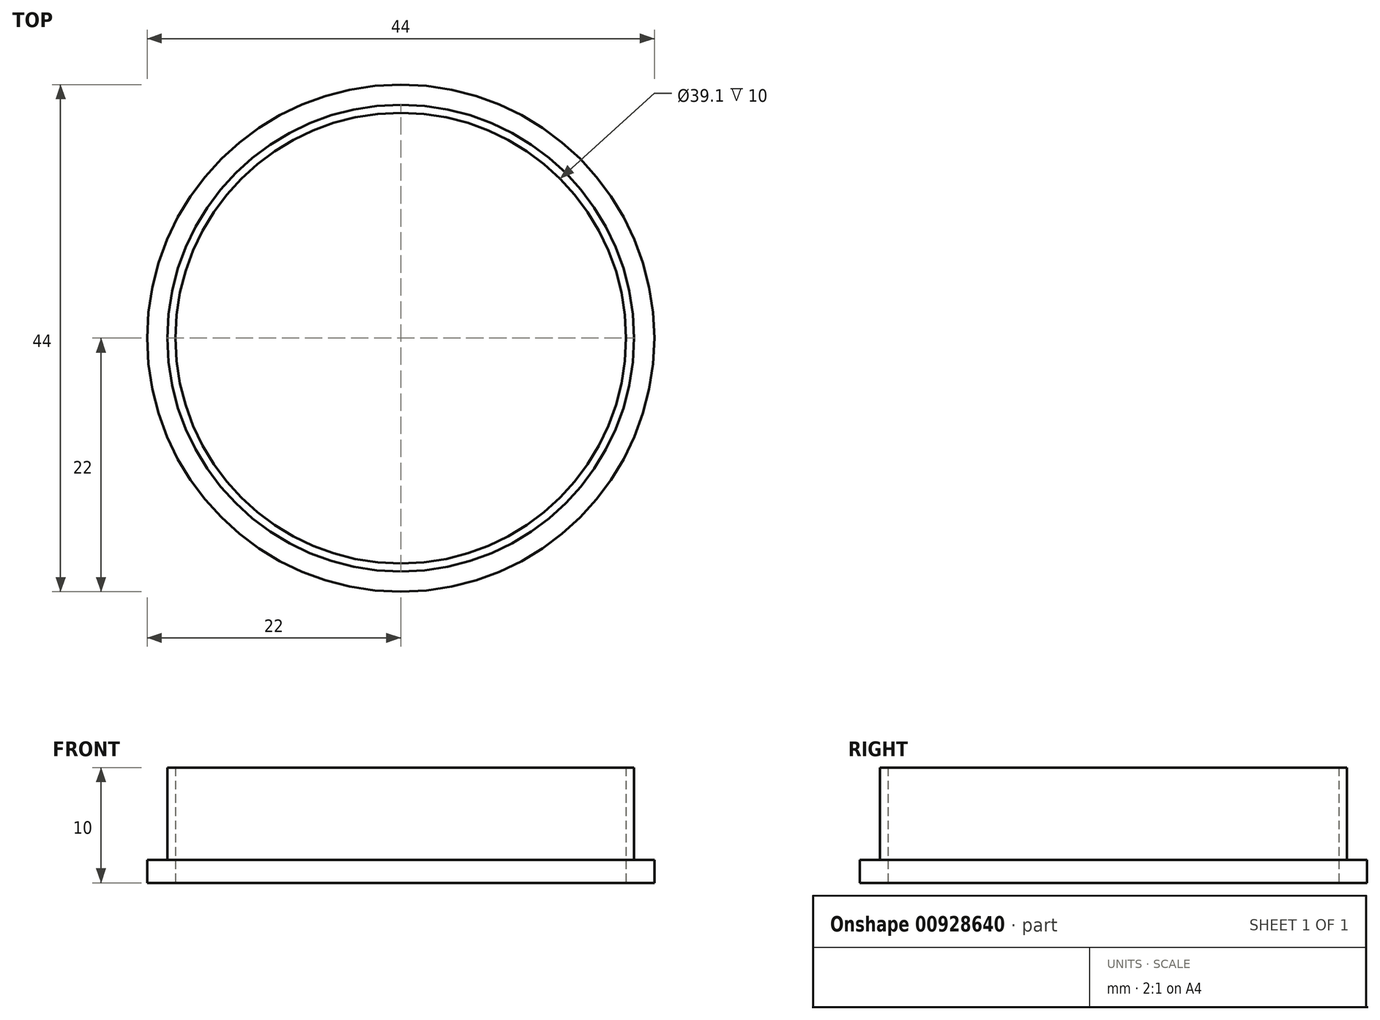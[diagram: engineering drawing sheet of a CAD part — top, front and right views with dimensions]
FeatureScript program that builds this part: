
annotation { "Feature Type Name" : "Feature", "Feature Type Description" : "" }
export const myFeature = defineFeature(function(context is Context, id is Id, definition is map)
    precondition{}
    {
        {
            var Q0;
            Q0=qCreatedBy(makeId("Top.planeOp"),FACE);
            var sketch = newSketch(context, id + "F0", { "sketchPlane" : qUnion([Q0])});
            skCircle(sketch, "E0", {"center": v(0, 0) * mm, "radius": 20.25 * mm});
            skSolve(sketch);
        }
        {
            var Q0;
            Q0=qCreatedBy(makeId("Top.planeOp"),FACE);
            var sketch = newSketch(context, id + "F1", { "sketchPlane" : qUnion([Q0])});
            skCircle(sketch, "E1", {"center": v(0, 0) * mm, "radius": 19.55 * mm});
            skSolve(sketch);
        }
        {
            var Q0;
            Q0=qCreatedBy(makeId("Top.planeOp"),FACE);
            var sketch = newSketch(context, id + "F2", { "sketchPlane" : qUnion([Q0])});
            skCircle(sketch, "E2", {"center": v(0, 0) * mm, "radius": 22 * mm});
            skSolve(sketch);
        }
        {
            var Q0;
            Q0 = qSketchRegion(id + "F2", true);
            extrude(context, id + "F3", {"entities" : qUnion([Q0]), "depth" : 2 * mm, "offsetDistance" : 25 * mm});
        }
        {
            var Q0;
            Q0 = qSketchRegion(id + "F0", true);
            extrude(context, id + "F4", {"entities" : qUnion([Q0]), "operationType" : NewBodyOperationType.ADD, "depth" : 10 * mm, "offsetDistance" : 25 * mm});
        }
        {
            var Q0;
            Q0 = qSketchRegion(id + "F1", true);
            extrude(context, id + "F5", {"entities" : qUnion([Q0]), "operationType" : NewBodyOperationType.REMOVE, "depth" : 10 * mm, "offsetDistance" : 25 * mm});
        }
    });
